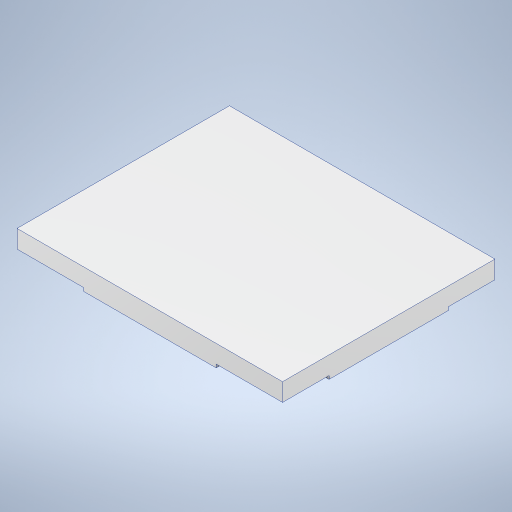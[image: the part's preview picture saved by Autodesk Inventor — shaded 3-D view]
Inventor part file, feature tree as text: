
AUTODESK INVENTOR PART (.ipt)
format: ipt  version: 2024 (Build 280153000, 153)  size: 303,104 bytes
history: native  units: mm
features: extrude x6, sketch x6, fillet x2, projected_geometry x1
ambient origin geometry x8: Origin, YZ Plane, XZ Plane, XY Plane, X Axis, Y Axis, Z Axis, Center Point
bodies: Solid1 (feature_tree)
feature tree (15):
  extrude  "Extrusion1"  Depth=200.0mm
  extrude  "Extrusion2"  Depth=60.0mm
  extrude  "Extrusion3"  Depth=12.0mm
  extrude  "Extrusion6"  Depth=5.0mm TaperAngle=0.0deg
  fillet  "Fillet1"  Radius=12.0mm
  fillet  "Fillet2"  Radius=25.0mm
  extrude  "Extrusion7"  Depth=50.0mm
  extrude  "Extrusion8"  Depth=50.0mm
  sketch  "Sketch1"  dims[d0=160.0mm d1=200.0mm]
  sketch  "Sketch2"  dims[d2=11.0mm d3=0.0mm d4=60.0mm]
  sketch  "Sketch3"  dims[d5=60.0mm d6=12.0mm]
  projected_geometry  "Projected Loop1"
  sketch  "Sketch7"  dims[d7=10.0mm d8=0.0mm d9=5.0mm d10=0.0mm d17=12.0mm d18=25.0mm]
  sketch  "Sketch8"  dims[d19=25.0mm d20=50.0mm]
  sketch  "Sketch10"  dims[d21=50.0mm d22=50.0mm d23=50.0mm d24=10.0mm d25=0.0mm d26=4.0mm d27=10.0mm d28=1000.0mm d29=0.0mm d30=50.0mm d31=50.0mm d32=50.0mm d33=50.0mm d34=35.0mm d35=35.0mm d36=0.0mm d37=2.5mm d38=0.0mm]
